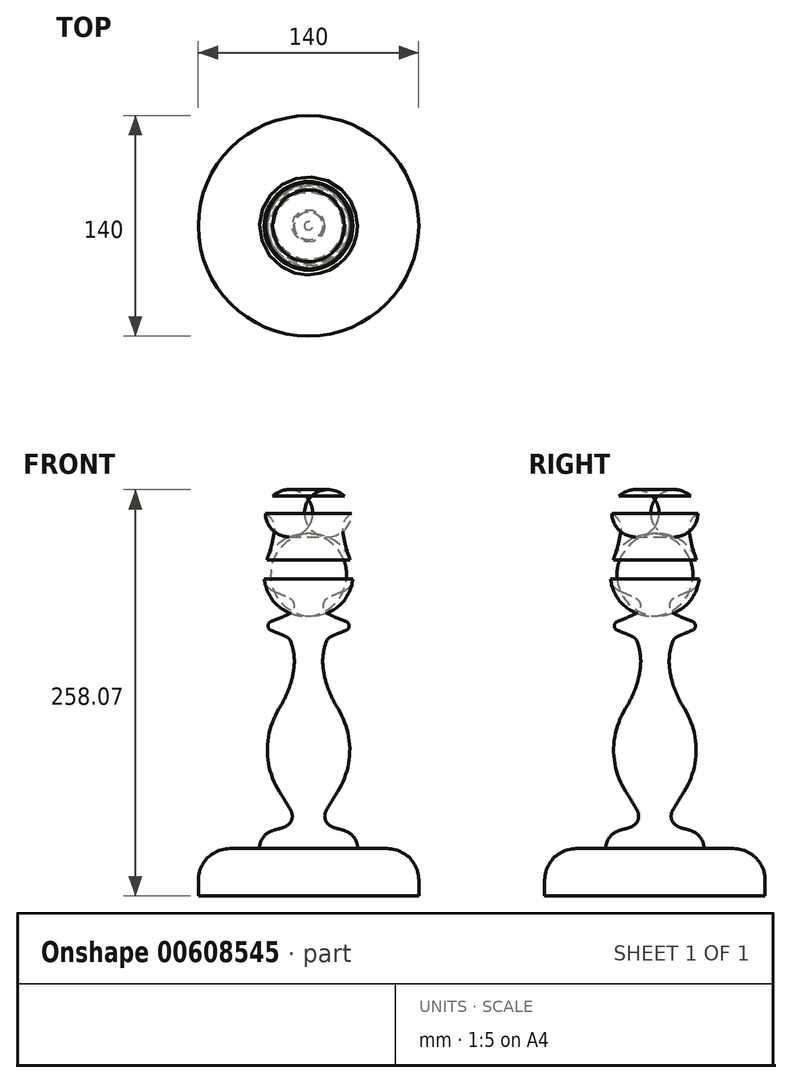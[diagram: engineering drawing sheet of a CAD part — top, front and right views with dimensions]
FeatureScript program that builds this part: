
annotation { "Feature Type Name" : "Feature", "Feature Type Description" : "" }
export const myFeature = defineFeature(function(context is Context, id is Id, definition is map)
    precondition{}
    {
        {
            var Q0;
            Q0=qCreatedBy(makeId("Front.planeOp"),FACE);
            var sketch = newSketch(context, id + "F0", { "sketchPlane" : qUnion([Q0])});
            skLineSegment(sketch, "E0", {"start": v(55.12, 284.36) * mm, "end": v(113.14, 284.36) * mm});
            skArc(sketch, "E1", {"start": v(65.46, 149.46) * mm, "mid": v(57.93, 123) * mm, "end": v(65.7, 96.6) * mm});
            skArc(sketch, "E2", {"start": v(65.7, 96.6) * mm, "mid": v(69.38, 90.64) * mm, "end": v(72.92, 84.58) * mm});
            skArc(sketch, "E3", {"start": v(72.92, 84.58) * mm, "mid": v(73.65, 79.54) * mm, "end": v(70.8, 75.32) * mm});
            skArc(sketch, "E4", {"start": v(65.46, 149.46) * mm, "mid": v(68.78, 155.4) * mm, "end": v(71.5, 161.65) * mm});
            skArc(sketch, "E5", {"start": v(71.5, 161.65) * mm, "mid": v(73.62, 168.42) * mm, "end": v(74.87, 175.4) * mm});
            skArc(sketch, "E6", {"start": v(70.8, 75.32) * mm, "mid": v(68.32, 73.96) * mm, "end": v(65.61, 73.13) * mm});
            skArc(sketch, "E7", {"start": v(65.61, 73.13) * mm, "mid": v(62.39, 72.28) * mm, "end": v(59.3, 71) * mm});
            skArc(sketch, "E8", {"start": v(59.3, 71) * mm, "mid": v(54.62, 66.66) * mm, "end": v(53.03, 60.48) * mm});
            skLineSegment(sketch, "E9", {"start": v(53.03, 60.48) * mm, "end": v(105.94, 60.48) * mm});
            skLineSegment(sketch, "E10", {"start": v(84.13, 284.36) * mm, "end": v(84.13, 60.48) * mm});
            skArc(sketch, "E11", {"start": v(62.42, 262.1) * mm, "mid": v(61.35, 268.58) * mm, "end": v(56.79, 273.32) * mm});
            skArc(sketch, "E12", {"start": v(57.67, 243.89) * mm, "mid": v(56.13, 237.96) * mm, "end": v(56, 231.84) * mm});
            skArc(sketch, "E13", {"start": v(57.67, 243.89) * mm, "mid": v(60.58, 252.85) * mm, "end": v(62.42, 262.1) * mm});
            skArc(sketch, "E14", {"start": v(56, 231.84) * mm, "mid": v(58.03, 226.8) * mm, "end": v(62.45, 223.67) * mm});
            skArc(sketch, "E15", {"start": v(62.45, 223.67) * mm, "mid": v(67.26, 221.82) * mm, "end": v(71.93, 219.63) * mm});
            skArc(sketch, "E16", {"start": v(71.93, 219.63) * mm, "mid": v(74.93, 214.71) * mm, "end": v(71.93, 209.8) * mm});
            skArc(sketch, "E17", {"start": v(71.93, 209.8) * mm, "mid": v(61.77, 205.28) * mm, "end": v(51.16, 201.93) * mm});
            skArc(sketch, "E18.MirrorCS", {"start": v(70.25, 194.9) * mm, "mid": v(60.89, 198.9) * mm, "end": v(51.16, 201.93) * mm});
            skArc(sketch, "E19", {"start": v(74.87, 175.4) * mm, "mid": v(74.82, 183.95) * mm, "end": v(72.7, 192.24) * mm});
            skPoint(sketch, "E20.visualSharp", {"position": v(71.93, 194.06) * mm});
            skArc(sketch, "E20.filletArc", {"start": v(72.7, 192.24) * mm, "mid": v(71.73, 193.8) * mm, "end": v(70.25, 194.9) * mm});
            skArc(sketch, "E21", {"start": v(61.39, 284.36) * mm, "mid": v(57.94, 279.32) * mm, "end": v(56.79, 273.32) * mm});
            skSolve(sketch);
        }
        {
            var Q0;
            Q0=makeQuery(id+"F0.imprint","IMPRINT",FACE,{"disambiguationData":[TD([[makeQuery(id+"F0.imprint","IMPRINT",EDGE,{"derivedFrom":sQuery(id+"F0.wireOp",EDGE,"E1")}),1.0]])]});
            var Q1;
            Q1=sQuery(id+"F0.wireOp",EDGE,"E10");
            revolve(context, id + "F1", {"entities" : qUnion([Q0]), "axis" : qUnion([Q1]), "revolveType" : RevolveType.FULL});
        }
        {
            var Q0;
            Q0=makeQuery(id+"F1.opRevolve","SWEPT_EDGE",EDGE,{"disambiguationData":[OSD([sQuery(id+"F0.wireOp",EDGE,"E17"),sQuery(id+"F0.wireOp",EDGE,"E18.MirrorCS")])]});
            fillet(context, id + "F2", {"entities" : qUnion([Q0]), "radius" : 3 * mm, "tangentPropagation" : true, "allowEdgeOverflow" : false});
        }
        {
            var Q0;
            Q0=qCreatedBy(makeId("Front.planeOp"),FACE);
            var sketch = newSketch(context, id + "F3", { "sketchPlane" : qUnion([Q0])});
            skLineSegment(sketch, "E22.0", {"start": v(53.03, 60.48) * mm, "end": v(134.13, 60.48) * mm});
            skLineSegment(sketch, "E23", {"start": v(84.13, 60.48) * mm, "end": v(84.13, 14.83) * mm});
            skLineSegment(sketch, "E24", {"start": v(50.33, 30.48) * mm, "end": v(154.13, 30.48) * mm});
            skLineSegment(sketch, "E25", {"start": v(154.13, 30.48) * mm, "end": v(154.13, 40.48) * mm});
            skPoint(sketch, "E26.orphan", {"position": v(115.24, 60.48) * mm});
            skArc(sketch, "E27.filletArc", {"start": v(154.13, 40.48) * mm, "mid": v(148.27, 54.62) * mm, "end": v(134.13, 60.48) * mm});
            skSolve(sketch);
        }
        {
            var Q0;
            {var subQ0=sQuery(id+"F3.wireOp",EDGE,"E25");Q0=makeQuery(id+"F3.imprint","IMPRINT",FACE,{"disambiguationData":[TD([[makeQuery(id+"F3.imprint","IMPRINT",EDGE,{"derivedFrom":subQ0}),1.0]])]});}
            var Q1;
            Q1=sQuery(id+"F3.wireOp",EDGE,"E23");
            revolve(context, id + "F4", {"entities" : qUnion([Q0]), "axis" : qUnion([Q1]), "revolveType" : RevolveType.FULL});
        }
    });
